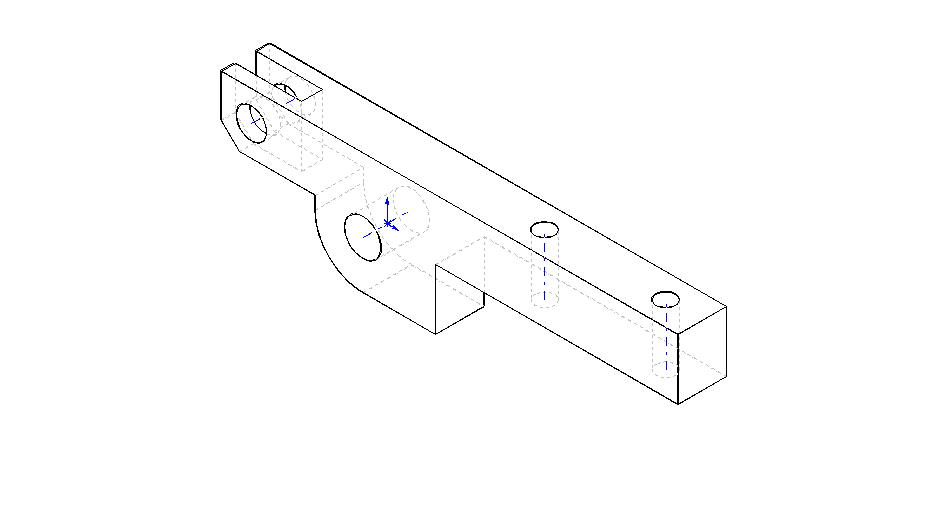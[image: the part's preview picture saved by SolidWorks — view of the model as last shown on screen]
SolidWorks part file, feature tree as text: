
SOLIDWORKS PART (.sldprt)
format: sldprt  version: not decoded by parser v0  size: 179,712 bytes
history: native  units: mm
features: sketch x4, plane x3, cut_extrude x2, thread x2, material x1, extrude x1, chamfer x1 (+8 scaffold rows collapsed)
feature tree (22):
  scaffold x8  (default folders/planes/origin — collapsed)
  material  "Matériau <non spécifié>"
  plane  "Face"
  plane  "Dessus"
  plane  "Droite"
  sketch  "Esquisse1"  dims[c1.D1=6.0mm c1.D2=5.0mm c1.D3=5.0mm c1.D4=5.0mm c1.D9=5.0mm c1.D11=7.9mm c2.D3=18.4mm c2.D4=7.1mm c2.D5=5.0mm c2.D6=75.4mm c2.D7=40.0mm c2.D8=10.0mm c2.D9=5.0mm c2.D10=10.0mm]
  extrude  "Base-Extrusion"  Depth=8mm
  chamfer  "Chanfrein1"  Distance=3mm Angle=45deg
  sketch  "Esquisse2"  dims[D2=6.0mm D1=0.0mm]
  cut_extrude  "Enlèv. mat.-Extru.2"  Depth=3.5mm
  sketch  "Esquisse7"  dims[c1.D1=3.2mm c1.D2=3.2mm c1.D3=3.2mm c2.D2=6.0mm c2.D3=20.0mm c3.D2=26.0mm]
  cut_extrude  "Enlèv. mat.-Extru.3"  [1 undecoded]
  thread  "Représentation de filetage1"  Diameter=4mm  [1 undecoded]
  thread  "Représentation de filetage2"  Diameter=4mm  [1 undecoded]
  sketch  "Point doigt"  dims[D1=35.0mm]
decode coverage: 9 of 10 modeling features carry decoded parameters
note: 3 parameter values undecoded
note: suppression state not decoded; provenance and decode notes live in map.json
